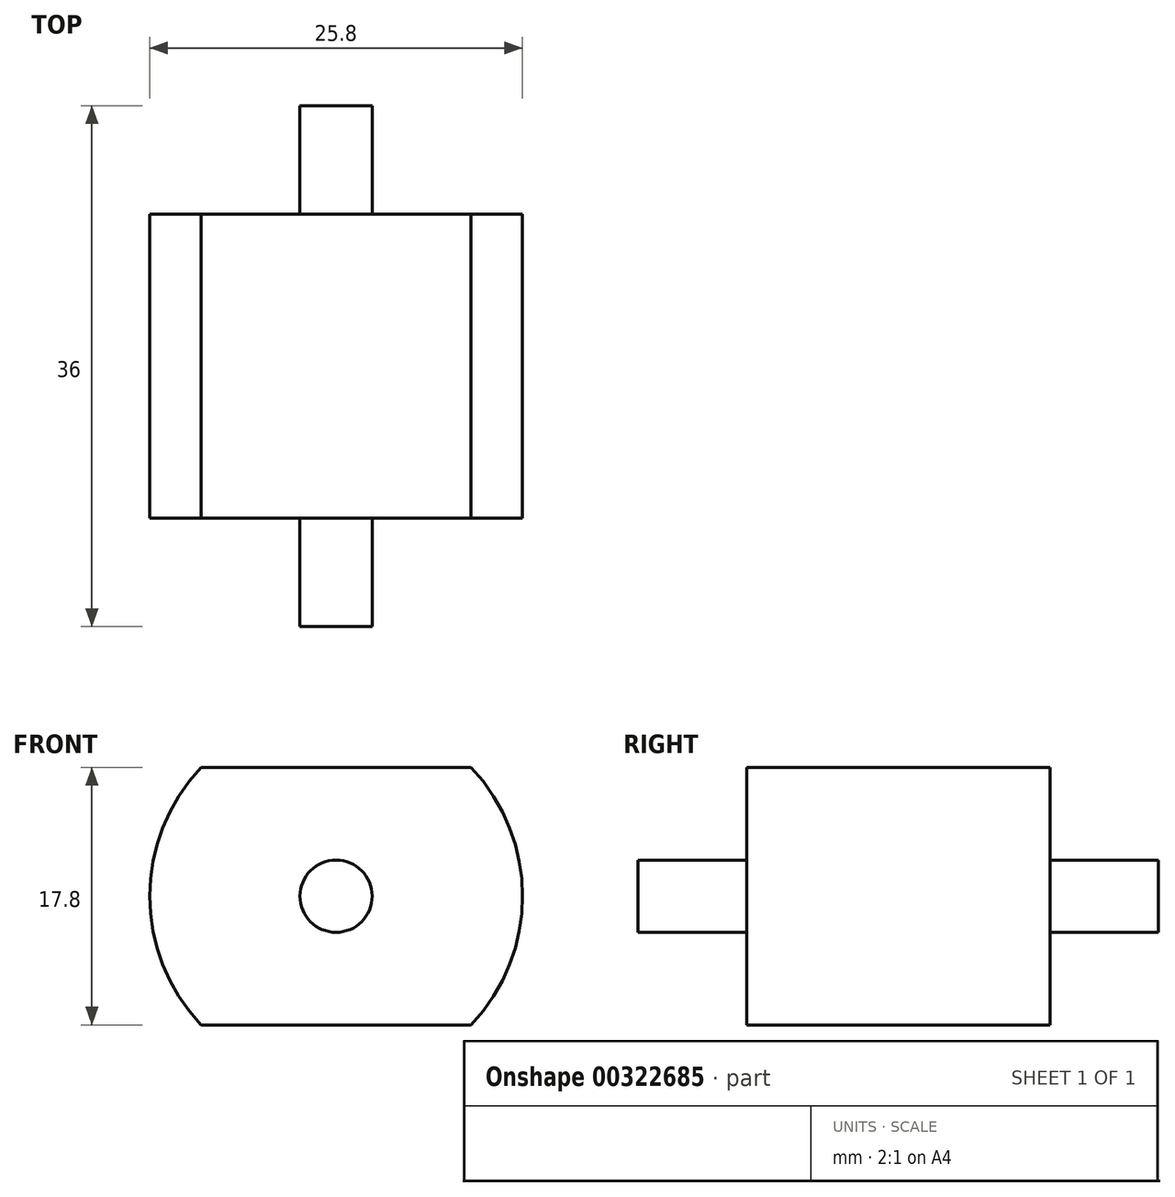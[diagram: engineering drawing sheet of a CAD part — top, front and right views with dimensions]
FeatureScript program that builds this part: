
annotation { "Feature Type Name" : "Feature", "Feature Type Description" : "" }
export const myFeature = defineFeature(function(context is Context, id is Id, definition is map)
    precondition{}
    {
        {
            var Q0;
            Q0=qCreatedBy(makeId("Front.planeOp"),FACE);
            var sketch = newSketch(context, id + "F0", { "sketchPlane" : qUnion([Q0])});
            skArc(sketch, "E0", {"start": v(-9.34, 8.9) * mm, "mid": v(-12.9, 0) * mm, "end": v(-9.34, -8.9) * mm});
            skLineSegment(sketch, "E1", {"start": v(-9.34, 8.9) * mm, "end": v(9.34, 8.9) * mm});
            skLineSegment(sketch, "E2", {"start": v(-9.34, -8.9) * mm, "end": v(9.34, -8.9) * mm});
            skArc(sketch, "E3.trimOffspring", {"start": v(9.34, -8.9) * mm, "mid": v(12.9, 0) * mm, "end": v(9.34, 8.9) * mm});
            skCircle(sketch, "E4", {"center": v(0, 0) * mm, "radius": 2.5 * mm});
            skSolve(sketch);
        }
        {
            var Q0;
            Q0=makeQuery(id+"F0.imprint","IMPRINT",FACE,{"disambiguationData":[TD([[makeQuery(id+"F0.imprint","IMPRINT",EDGE,{"derivedFrom":sQuery(id+"F0.wireOp",EDGE,"E4")}),1.0]])]});
            extrude(context, id + "F1", {"entities" : qUnion([Q0]), "depth" : 36 * mm, "symmetric" : true});
        }
        {
            var Q0;
            Q0=makeQuery(id+"F0.imprint","IMPRINT",FACE,{"disambiguationData":[TD([[makeQuery(id+"F0.imprint","IMPRINT",EDGE,{"derivedFrom":sQuery(id+"F0.wireOp",EDGE,"E0")}),1.0]])]});
            extrude(context, id + "F2", {"entities" : qUnion([Q0]), "operationType" : NewBodyOperationType.ADD, "depth" : 21 * mm, "symmetric" : true});
        }
    });
